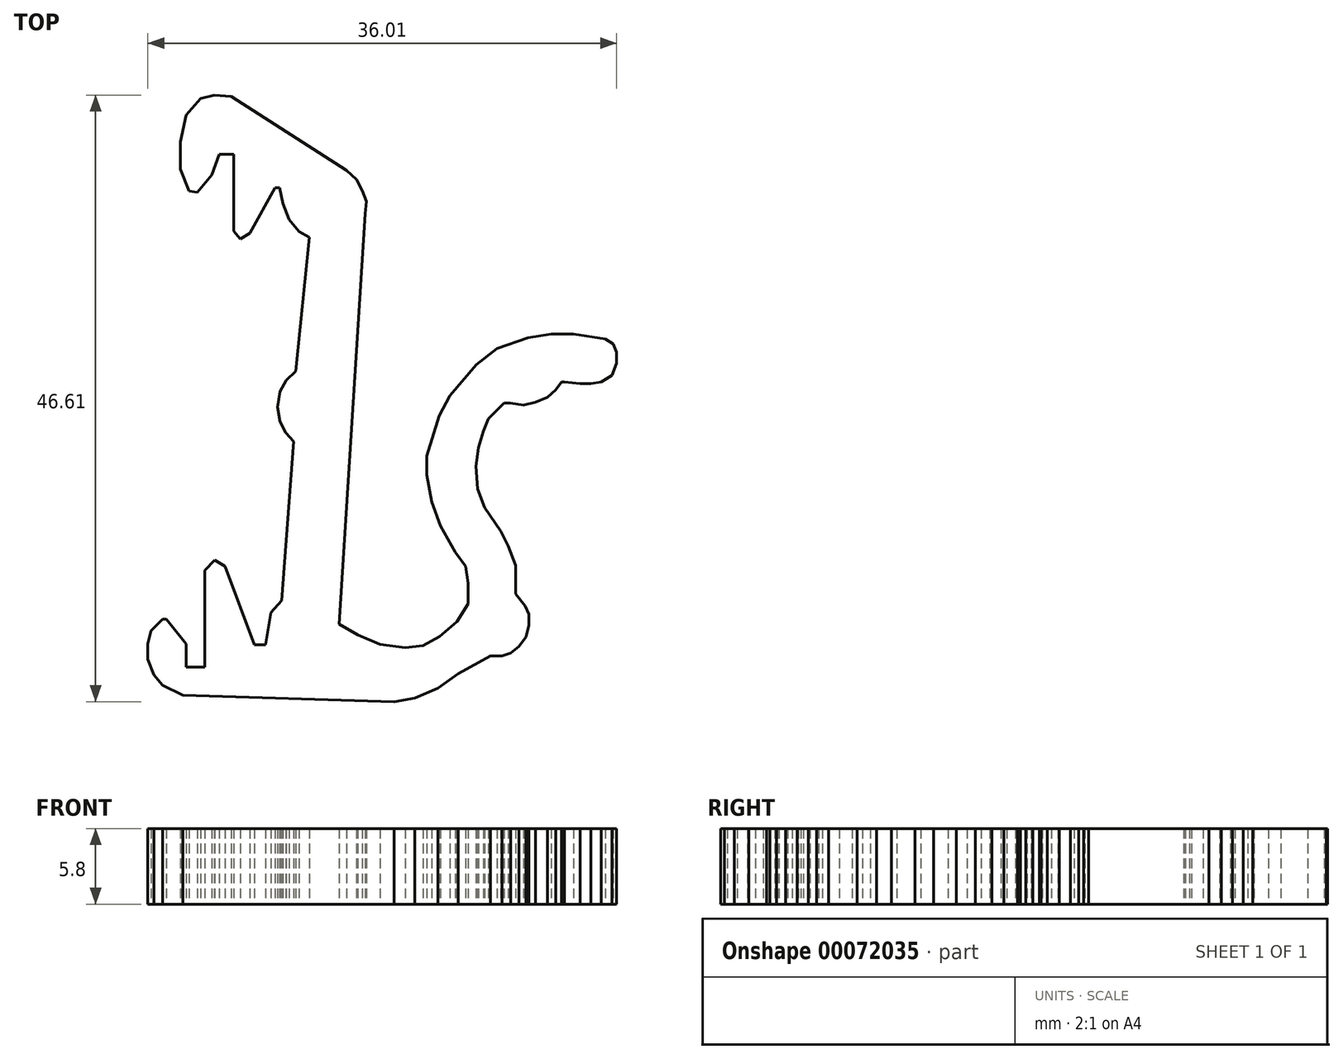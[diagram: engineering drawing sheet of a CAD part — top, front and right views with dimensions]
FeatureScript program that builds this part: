
annotation { "Feature Type Name" : "Feature", "Feature Type Description" : "" }
export const myFeature = defineFeature(function(context is Context, id is Id, definition is map)
    precondition{}
    {
        {
            var Q0;
            Q0=qCreatedBy(makeId("Top.planeOp"),FACE);
            var sketch = newSketch(context, id + "F0", { "sketchPlane" : qUnion([Q0])});
            skLineSegment(sketch, "E0", {"start": v(11, 25.83) * mm, "end": v(19.87, 20.17) * mm});
            skLineSegment(sketch, "E1", {"start": v(19.87, 20.17) * mm, "end": v(20.6, 19.45) * mm});
            skLineSegment(sketch, "E2", {"start": v(20.6, 19.45) * mm, "end": v(21.06, 18.62) * mm});
            skLineSegment(sketch, "E3", {"start": v(21.06, 18.62) * mm, "end": v(21.38, 17.77) * mm});
            skLineSegment(sketch, "E4", {"start": v(21.38, 17.77) * mm, "end": v(21.28, 16.82) * mm});
            skLineSegment(sketch, "E5", {"start": v(21.28, 16.82) * mm, "end": v(19.3, -14.72) * mm});
            skLineSegment(sketch, "E6", {"start": v(19.3, -14.72) * mm, "end": v(20.7, -15.53) * mm});
            skLineSegment(sketch, "E7", {"start": v(20.7, -15.53) * mm, "end": v(22.44, -16.26) * mm});
            skLineSegment(sketch, "E8", {"start": v(22.44, -16.26) * mm, "end": v(24.37, -16.52) * mm});
            skLineSegment(sketch, "E9", {"start": v(24.37, -16.52) * mm, "end": v(25.72, -16.35) * mm});
            skLineSegment(sketch, "E10", {"start": v(25.72, -16.35) * mm, "end": v(27, -15.65) * mm});
            skLineSegment(sketch, "E11", {"start": v(27, -15.65) * mm, "end": v(28.33, -14.5) * mm});
            skLineSegment(sketch, "E12", {"start": v(28.33, -14.5) * mm, "end": v(29.2, -13.16) * mm});
            skLineSegment(sketch, "E13", {"start": v(29.2, -13.16) * mm, "end": v(29.2, -11.57) * mm});
            skLineSegment(sketch, "E14", {"start": v(29.2, -11.57) * mm, "end": v(29, -10.26) * mm});
            skLineSegment(sketch, "E15", {"start": v(29, -10.26) * mm, "end": v(28.2, -9.18) * mm});
            skLineSegment(sketch, "E16", {"start": v(28.2, -9.18) * mm, "end": v(27.07, -7.15) * mm});
            skLineSegment(sketch, "E17", {"start": v(27.07, -7.15) * mm, "end": v(26.4, -5.3) * mm});
            skLineSegment(sketch, "E18", {"start": v(26.4, -5.3) * mm, "end": v(26, -3.23) * mm});
            skLineSegment(sketch, "E19", {"start": v(26, -3.23) * mm, "end": v(26, -1.77) * mm});
            skLineSegment(sketch, "E20", {"start": v(26, -1.77) * mm, "end": v(26.98, 1.29) * mm});
            skLineSegment(sketch, "E21", {"start": v(26.98, 1.29) * mm, "end": v(27.79, 2.84) * mm});
            skLineSegment(sketch, "E22", {"start": v(27.79, 2.84) * mm, "end": v(29.82, 5.23) * mm});
            skLineSegment(sketch, "E23", {"start": v(29.82, 5.23) * mm, "end": v(31.43, 6.46) * mm});
            skLineSegment(sketch, "E24", {"start": v(31.43, 6.46) * mm, "end": v(33.78, 7.3) * mm});
            skLineSegment(sketch, "E25", {"start": v(33.78, 7.3) * mm, "end": v(35.56, 7.58) * mm});
            skLineSegment(sketch, "E26", {"start": v(35.56, 7.58) * mm, "end": v(37.3, 7.58) * mm});
            skLineSegment(sketch, "E27", {"start": v(37.3, 7.58) * mm, "end": v(39.74, 7.19) * mm});
            skLineSegment(sketch, "E28", {"start": v(39.74, 7.19) * mm, "end": v(40.34, 6.83) * mm});
            skLineSegment(sketch, "E29", {"start": v(40.34, 6.83) * mm, "end": v(40.6, 6.2) * mm});
            skLineSegment(sketch, "E30", {"start": v(40.6, 6.2) * mm, "end": v(40.6, 5.33) * mm});
            skLineSegment(sketch, "E31", {"start": v(40.6, 5.33) * mm, "end": v(40.25, 4.4) * mm});
            skLineSegment(sketch, "E32", {"start": v(40.25, 4.4) * mm, "end": v(39.41, 3.92) * mm});
            skLineSegment(sketch, "E33", {"start": v(39.41, 3.92) * mm, "end": v(38.62, 3.79) * mm});
            skLineSegment(sketch, "E34", {"start": v(38.62, 3.79) * mm, "end": v(37.78, 3.79) * mm});
            skLineSegment(sketch, "E35", {"start": v(37.78, 3.79) * mm, "end": v(36.59, 3.89) * mm});
            skLineSegment(sketch, "E36", {"start": v(36.59, 3.89) * mm, "end": v(36.37, 3.89) * mm});
            skLineSegment(sketch, "E37", {"start": v(36.37, 3.89) * mm, "end": v(35.91, 3.3) * mm});
            skLineSegment(sketch, "E38", {"start": v(35.91, 3.3) * mm, "end": v(35.27, 2.74) * mm});
            skLineSegment(sketch, "E39", {"start": v(35.27, 2.74) * mm, "end": v(34.36, 2.33) * mm});
            skLineSegment(sketch, "E40", {"start": v(34.36, 2.33) * mm, "end": v(33.43, 2.13) * mm});
            skLineSegment(sketch, "E41", {"start": v(33.43, 2.13) * mm, "end": v(32.44, 2.29) * mm});
            skLineSegment(sketch, "E42", {"start": v(32.44, 2.29) * mm, "end": v(31.95, 2.29) * mm});
            skLineSegment(sketch, "E43", {"start": v(31.95, 2.29) * mm, "end": v(30.75, 1.08) * mm});
            skLineSegment(sketch, "E44", {"start": v(30.75, 1.08) * mm, "end": v(30.37, 0.14) * mm});
            skLineSegment(sketch, "E45", {"start": v(30.37, 0.14) * mm, "end": v(29.98, -1.14) * mm});
            skLineSegment(sketch, "E46", {"start": v(29.98, -1.14) * mm, "end": v(29.78, -2.57) * mm});
            skLineSegment(sketch, "E47", {"start": v(29.78, -2.57) * mm, "end": v(29.92, -4.33) * mm});
            skLineSegment(sketch, "E48", {"start": v(29.92, -4.33) * mm, "end": v(30.46, -5.74) * mm});
            skLineSegment(sketch, "E49", {"start": v(30.46, -5.74) * mm, "end": v(31.7, -7.55) * mm});
            skLineSegment(sketch, "E50", {"start": v(31.7, -7.55) * mm, "end": v(32.29, -8.7) * mm});
            skLineSegment(sketch, "E51", {"start": v(32.29, -8.7) * mm, "end": v(32.85, -10.2) * mm});
            skLineSegment(sketch, "E52", {"start": v(32.85, -10.2) * mm, "end": v(32.85, -11.6) * mm});
            skLineSegment(sketch, "E53", {"start": v(32.85, -11.6) * mm, "end": v(32.85, -12.39) * mm});
            skLineSegment(sketch, "E54", {"start": v(32.85, -12.39) * mm, "end": v(33.58, -13.3) * mm});
            skLineSegment(sketch, "E55", {"start": v(33.58, -13.3) * mm, "end": v(33.87, -13.93) * mm});
            skLineSegment(sketch, "E56", {"start": v(33.87, -13.93) * mm, "end": v(33.87, -14.8) * mm});
            skLineSegment(sketch, "E57", {"start": v(33.87, -14.8) * mm, "end": v(33.63, -15.7) * mm});
            skLineSegment(sketch, "E58", {"start": v(33.63, -15.7) * mm, "end": v(33.1, -16.4) * mm});
            skLineSegment(sketch, "E59", {"start": v(33.1, -16.4) * mm, "end": v(32.47, -16.91) * mm});
            skLineSegment(sketch, "E60", {"start": v(32.47, -16.91) * mm, "end": v(31.8, -17.16) * mm});
            skLineSegment(sketch, "E61", {"start": v(31.8, -17.16) * mm, "end": v(30.9, -17.16) * mm});
            skLineSegment(sketch, "E62", {"start": v(30.9, -17.16) * mm, "end": v(28.43, -18.53) * mm});
            skLineSegment(sketch, "E63", {"start": v(28.43, -18.53) * mm, "end": v(26.86, -19.64) * mm});
            skLineSegment(sketch, "E64", {"start": v(26.86, -19.64) * mm, "end": v(25.1, -20.39) * mm});
            skLineSegment(sketch, "E65", {"start": v(25.1, -20.39) * mm, "end": v(23.51, -20.67) * mm});
            skLineSegment(sketch, "E66", {"start": v(23.51, -20.67) * mm, "end": v(7.29, -20.18) * mm});
            skLineSegment(sketch, "E67", {"start": v(7.29, -20.18) * mm, "end": v(5.72, -19.4) * mm});
            skLineSegment(sketch, "E68", {"start": v(5.72, -19.4) * mm, "end": v(5.07, -18.6) * mm});
            skLineSegment(sketch, "E69", {"start": v(5.07, -18.6) * mm, "end": v(4.59, -17.4) * mm});
            skLineSegment(sketch, "E70", {"start": v(4.59, -17.4) * mm, "end": v(4.59, -16.22) * mm});
            skLineSegment(sketch, "E71", {"start": v(4.59, -16.22) * mm, "end": v(4.84, -15.2) * mm});
            skLineSegment(sketch, "E72", {"start": v(4.84, -15.2) * mm, "end": v(5.72, -14.34) * mm});
            skLineSegment(sketch, "E73", {"start": v(5.72, -14.34) * mm, "end": v(6, -14.34) * mm});
            skLineSegment(sketch, "E74", {"start": v(6, -14.34) * mm, "end": v(7.53, -16.24) * mm});
            skLineSegment(sketch, "E75", {"start": v(8.96, -18.01) * mm, "end": v(8.96, -10.58) * mm});
            skLineSegment(sketch, "E76", {"start": v(8.96, -10.58) * mm, "end": v(9.74, -9.78) * mm});
            skLineSegment(sketch, "E77", {"start": v(9.74, -9.78) * mm, "end": v(10.52, -10.25) * mm});
            skLineSegment(sketch, "E78", {"start": v(10.52, -10.25) * mm, "end": v(12.79, -16.3) * mm});
            skLineSegment(sketch, "E79", {"start": v(12.79, -16.3) * mm, "end": v(13.62, -16.3) * mm});
            skLineSegment(sketch, "E80", {"start": v(13.62, -16.3) * mm, "end": v(14.06, -13.8) * mm});
            skLineSegment(sketch, "E81", {"start": v(14.06, -13.8) * mm, "end": v(14.86, -12.88) * mm});
            skLineSegment(sketch, "E82", {"start": v(14.86, -12.88) * mm, "end": v(15.8, -0.68) * mm});
            skLineSegment(sketch, "E83", {"start": v(15.8, -0.68) * mm, "end": v(15.18, 0) * mm});
            skLineSegment(sketch, "E84", {"start": v(15.18, 0) * mm, "end": v(14.73, 0.85) * mm});
            skLineSegment(sketch, "E85", {"start": v(14.73, 0.85) * mm, "end": v(14.54, 1.96) * mm});
            skLineSegment(sketch, "E86", {"start": v(14.54, 1.96) * mm, "end": v(14.73, 3.16) * mm});
            skLineSegment(sketch, "E87", {"start": v(14.73, 3.16) * mm, "end": v(15.23, 4.02) * mm});
            skLineSegment(sketch, "E88", {"start": v(15.23, 4.02) * mm, "end": v(15.96, 4.72) * mm});
            skLineSegment(sketch, "E89", {"start": v(15.96, 4.72) * mm, "end": v(16.99, 15) * mm});
            skLineSegment(sketch, "E90", {"start": v(16.99, 15) * mm, "end": v(16.2, 15.47) * mm});
            skLineSegment(sketch, "E91", {"start": v(16.2, 15.47) * mm, "end": v(15.44, 16.37) * mm});
            skLineSegment(sketch, "E92", {"start": v(15.44, 16.37) * mm, "end": v(14.97, 17.63) * mm});
            skLineSegment(sketch, "E93", {"start": v(14.97, 17.63) * mm, "end": v(14.71, 18.83) * mm});
            skLineSegment(sketch, "E94", {"start": v(14.71, 18.83) * mm, "end": v(14.36, 18.83) * mm});
            skLineSegment(sketch, "E95", {"start": v(14.36, 18.83) * mm, "end": v(12.43, 15.31) * mm});
            skLineSegment(sketch, "E96", {"start": v(12.43, 15.31) * mm, "end": v(11.71, 14.89) * mm});
            skLineSegment(sketch, "E97", {"start": v(11.71, 14.89) * mm, "end": v(11.18, 15.48) * mm});
            skLineSegment(sketch, "E98", {"start": v(11.18, 15.48) * mm, "end": v(11.18, 21.4) * mm});
            skLineSegment(sketch, "E99", {"start": v(11.18, 21.4) * mm, "end": v(10.1, 21.4) * mm});
            skLineSegment(sketch, "E100", {"start": v(10.1, 21.4) * mm, "end": v(9.52, 19.8) * mm});
            skLineSegment(sketch, "E101", {"start": v(9.52, 19.8) * mm, "end": v(8.4, 18.46) * mm});
            skLineSegment(sketch, "E102", {"start": v(8.4, 18.46) * mm, "end": v(7.75, 18.58) * mm});
            skLineSegment(sketch, "E103", {"start": v(7.75, 18.58) * mm, "end": v(7.1, 20.26) * mm});
            skLineSegment(sketch, "E104", {"start": v(7.1, 20.26) * mm, "end": v(7.1, 22.34) * mm});
            skLineSegment(sketch, "E105", {"start": v(7.1, 22.34) * mm, "end": v(7.55, 24.4) * mm});
            skLineSegment(sketch, "E106", {"start": v(7.55, 24.4) * mm, "end": v(8.64, 25.67) * mm});
            skLineSegment(sketch, "E107", {"start": v(8.64, 25.67) * mm, "end": v(9.71, 25.94) * mm});
            skLineSegment(sketch, "E108", {"start": v(9.71, 25.94) * mm, "end": v(11, 25.83) * mm});
            skLineSegment(sketch, "E109", {"start": v(7.53, -16.24) * mm, "end": v(7.53, -18.01) * mm});
            skLineSegment(sketch, "E110", {"start": v(7.53, -18.01) * mm, "end": v(8.96, -18.01) * mm});
            skSolve(sketch);
        }
        {
            var Q0;
            Q0=makeQuery(id+"F0.imprint","IMPRINT",FACE,{"disambiguationData":[TD([[makeQuery(id+"F0.imprint","IMPRINT",EDGE,{"derivedFrom":sQuery(id+"F0.wireOp",EDGE,"E0")}),-1.0]])]});
            extrude(context, id + "F1", {"entities" : qUnion([Q0]), "depth" : 5.8 * mm});
        }
    });
